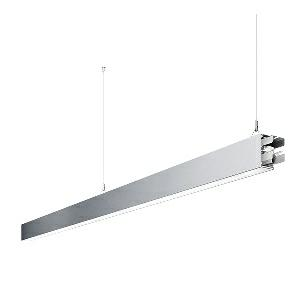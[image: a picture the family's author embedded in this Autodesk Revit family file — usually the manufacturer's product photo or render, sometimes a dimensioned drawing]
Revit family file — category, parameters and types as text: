
# Revit family: idoo_line_-_ilp_6000_830_d_mid_00805749_57ec
name_source: partatom
category: Lighting Fixtures
units: mm (PartAtom-declared; Revit-internal decimal feet)

## family parameters
Cut with Voids When Loaded = No
Host = Face
Light Source = No
Part Type = Normal
Room Calculation Point = No
Round Connector Dimension = Use Diameter
Shared = No

## types (1)
- IDOO.line - ILP 6000/830/D MID (1 x LED, 6000 lm, 3000K)
    Apparent Load = 46 VA
    Approval mark = CE
    CIE Flux Codes = 66 91 98 40 100
    Color Rendering = 80-89
    Color Temperature = 3000K
    Control Gear = Electronic ballast
    Default Elevation = 1800 mm
    Description = ILP 6000/830/D|Suspended luminaire|light source: LED|connected load: 220-240 V, 50/60 Hz|Power consumption: approx. 46 W|standby: approx. 0,15|luminous flux: 6000 lm|luminous efficacy: 130 lm/W|light distribution: Direct/indirect|direct ratio: approx. 40 %|colour temperature: Warm white, ca. 3000 K|color rendering index (CRI): >= 80|chromaticity tolerance:  3 SDCM|System of protection: IP 40|technology: Continuously dimmable|luminaire body|material: Sectional aluminium|colour: Silver|lamp cover: Acrylic (PMMA), Clear|mains lead: 1,0 m With free stranded wires|Fastening: Steel cable 0.3 - 0.7 m|glare control: Prism aperture|luminance(L65): <= 2700 cd/m|unified glare rating(4H 8H): <=  16|special features: DALI Load 1x, TouchDIM - dimming via standard switch, Through-wired, up to 18 m on one mains connection, Flicker-free, Suitable as emergency lighting, Mechanical and electrical connection of the individual modules without tools|
    Frequency = 50 Hz
    Height = 110 mm
    Lamp = 1 x LED
    Lamp Light Flux = 6000 lm
    Lamp count = 1
    Length = 2244 mm
    Luminous efficacy = 130 lm/W
    Manufacturer = Waldmann
    ModVariant = No
    Model = 00805749
    Mounting Place = Ceiling
    Mounting Type = Pendant
    Number of Poles = 1
    OnlyDefault = Yes
    Power Factor = 1
    Product Name = IDOO.line - ILP 6000/830/D MID
    Product group = Suspended luminaire
    ProductGroupID = 9
    Protection Class = Protection class I
    Protection Degree = IP 40
    RLX_Detail_Level = 1
    RLX_Emergency_Light_Flux = 0 lm
    RLX_Emergency_Type = 0
    RLX_Emergency_Type_DB = No
    RlxData = <blob elided: 24025 chars, md5=ec2011b8>
    Socket = socket
    Standby Power = 0 W
    System Light Flux = 6000 lm
    System Power = 46 W
    Type Comments = Product without accessories
    Type Image = 113317000-00692618.jpg
    URL = http://relux.com
    VarID = ---
    Voltage = 230 V
    Voltage Range = 220-240 V
    Weight = 0.00 kg
    Width = 60 mm  [stored 0.19685 ft]

note: [stored X ft] marks values corroborated as IEEE doubles in the binary element streams (Revit-internal decimal feet)

## geometry (parser evidence)
native form markers: Blend x4, Sweep x15
no freeform markers — native parametric forms only
